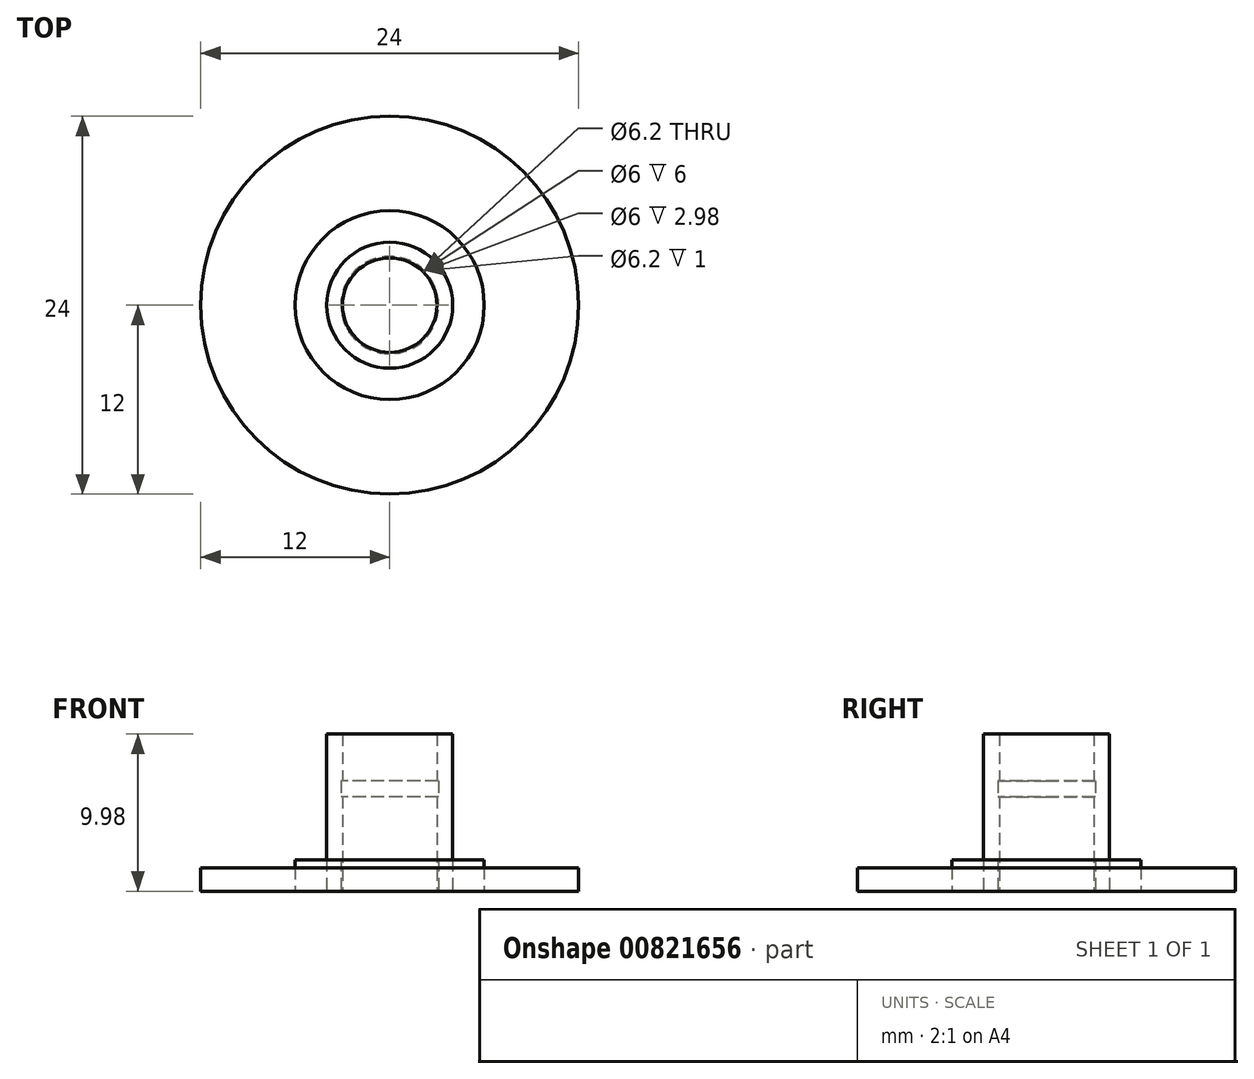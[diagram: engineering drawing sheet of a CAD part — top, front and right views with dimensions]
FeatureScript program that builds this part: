
annotation { "Feature Type Name" : "Feature", "Feature Type Description" : "" }
export const myFeature = defineFeature(function(context is Context, id is Id, definition is map)
    precondition{}
    {
        {
            var Q0;
            Q0=qCreatedBy(makeId("Top.planeOp"),FACE);
            var sketch = newSketch(context, id + "F0", { "sketchPlane" : qUnion([Q0])});
            skCircle(sketch, "E0", {"center": v(0, 0) * mm, "radius": 12 * mm});
            skCircle(sketch, "E1", {"center": v(0, 0) * mm, "radius": 3 * mm});
            skCircle(sketch, "E2", {"center": v(0, 0) * mm, "radius": 4 * mm});
            skCircle(sketch, "E3", {"center": v(0, 0) * mm, "radius": 6 * mm});
            skLineSegment(sketch, "E4", {"start": v(0, 0) * mm, "end": v(5.26, 2.9) * mm});
            skLineSegment(sketch, "E5", {"start": v(5.26, 2.9) * mm, "end": v(0, 0) * mm});
            skLineSegment(sketch, "E6", {"start": v(0, 0) * mm, "end": v(4.01, 4.46) * mm});
            skCircle(sketch, "E7", {"center": v(0, 0) * mm, "radius": 3.1 * mm});
            skSolve(sketch);
        }
        {
            var Q0;
            Q0=makeQuery(id+"F0.imprint","IMPRINT",FACE,{"disambiguationData":[TD([[makeQuery(id+"F0.imprint","IMPRINT",EDGE,{"derivedFrom":sQuery(id+"F0.wireOp",EDGE,"E0")}),1.0]])]});
            var Q1;
            Q1=makeQuery(id+"F0.imprint","IMPRINT",FACE,{"disambiguationData":[TD([[makeQuery(id+"F0.imprint","IMPRINT",EDGE,{"derivedFrom":sQuery(id+"F0.wireOp",EDGE,"E2")}),-1.0]])]});
            var Q2;
            Q2=makeQuery(id+"F0.imprint","IMPRINT",FACE,{"disambiguationData":[TD([[makeQuery(id+"F0.imprint","IMPRINT",EDGE,{"derivedFrom":sQuery(id+"F0.wireOp",EDGE,"E1")}),-1.0]])]});
            var Q3;
            Q3=makeQuery(id+"F0.imprint","IMPRINT",FACE,{"disambiguationData":[TD([[makeQuery(id+"F0.imprint","IMPRINT",EDGE,{"derivedFrom":sQuery(id+"F0.wireOp",EDGE,"E1")}),1.0]])]});
            var Q4;
            {var subQ0=sQuery(id+"F0.wireOp",EDGE,"E5");var subQ1=sQuery(id+"F0.wireOp",EDGE,"E2");var subQ2=makeQuery(id+"F0.imprint","INTERSECT",VERTEX,{"derivedFrom":[subQ1,subQ0]});Q4=makeQuery(id+"F0.imprint","IMPRINT",FACE,{"disambiguationData":[TD([[makeQuery(id+"F0.imprint","IMPRINT",EDGE,{"disambiguationData":[TD([[subQ2,1.0]])],"derivedFrom":subQ1}),1.0]])]});}
            var Q5;
            {var subQ0=sQuery(id+"F0.wireOp",EDGE,"E5");var subQ1=sQuery(id+"F0.wireOp",EDGE,"E2");var subQ2=makeQuery(id+"F0.imprint","INTERSECT",VERTEX,{"derivedFrom":[subQ1,subQ0]});Q5=makeQuery(id+"F0.imprint","IMPRINT",FACE,{"disambiguationData":[TD([[makeQuery(id+"F0.imprint","IMPRINT",EDGE,{"disambiguationData":[TD([[subQ2,-1.0]])],"derivedFrom":subQ1}),1.0]])]});}
            extrude(context, id + "F1", {"entities" : qUnion([Q0, Q1, Q2, Q3, Q4, Q5]), "depth" : 1.5 * mm, "offsetDistance" : 25 * mm});
        }
        {
            var Q0;
            Q0=makeQuery(id+"F0.imprint","IMPRINT",FACE,{"disambiguationData":[TD([[makeQuery(id+"F0.imprint","IMPRINT",EDGE,{"derivedFrom":sQuery(id+"F0.wireOp",EDGE,"E2")}),-1.0]])]});
            var Q1;
            {var subQ0=sQuery(id+"F0.wireOp",EDGE,"E5");var subQ1=sQuery(id+"F0.wireOp",EDGE,"E2");var subQ2=makeQuery(id+"F0.imprint","INTERSECT",VERTEX,{"derivedFrom":[subQ1,subQ0]});Q1=makeQuery(id+"F0.imprint","IMPRINT",FACE,{"disambiguationData":[TD([[makeQuery(id+"F0.imprint","IMPRINT",EDGE,{"disambiguationData":[TD([[subQ2,1.0]])],"derivedFrom":subQ1}),1.0]])]});}
            var Q2;
            {var subQ0=sQuery(id+"F0.wireOp",EDGE,"E5");var subQ1=sQuery(id+"F0.wireOp",EDGE,"E2");var subQ2=makeQuery(id+"F0.imprint","INTERSECT",VERTEX,{"derivedFrom":[subQ1,subQ0]});Q2=makeQuery(id+"F0.imprint","IMPRINT",FACE,{"disambiguationData":[TD([[makeQuery(id+"F0.imprint","IMPRINT",EDGE,{"disambiguationData":[TD([[subQ2,-1.0]])],"derivedFrom":subQ1}),1.0]])]});}
            extrude(context, id + "F2", {"entities" : qUnion([Q0, Q1, Q2]), "depth" : 2 * mm, "offsetDistance" : 25 * mm});
        }
        {
            var Q0;
            {var subQ0=sQuery(id+"F0.wireOp",EDGE,"E5");var subQ1=sQuery(id+"F0.wireOp",EDGE,"E1");var subQ2=makeQuery(id+"F0.imprint","INTERSECT",VERTEX,{"derivedFrom":[subQ1,subQ0]});Q0=makeQuery(id+"F0.imprint","IMPRINT",FACE,{"disambiguationData":[TD([[makeQuery(id+"F0.imprint","IMPRINT",EDGE,{"disambiguationData":[TD([[subQ2,1.0]])],"derivedFrom":subQ1}),-1.0]])]});}
            var Q1;
            {var subQ0=sQuery(id+"F0.wireOp",EDGE,"E5");var subQ1=sQuery(id+"F0.wireOp",EDGE,"E2");var subQ2=makeQuery(id+"F0.imprint","INTERSECT",VERTEX,{"derivedFrom":[subQ1,subQ0]});Q1=makeQuery(id+"F0.imprint","IMPRINT",FACE,{"disambiguationData":[TD([[makeQuery(id+"F0.imprint","IMPRINT",EDGE,{"disambiguationData":[TD([[subQ2,1.0]])],"derivedFrom":subQ1}),1.0]])]});}
            extrude(context, id + "F3", {"entities" : qUnion([Q0, Q1]), "depth" : 9.98 * mm, "offsetDistance" : 25 * mm});
        }
        {
            var Q0;
            {var subQ0=sQuery(id+"F0.wireOp",EDGE,"E5");var subQ1=sQuery(id+"F0.wireOp",EDGE,"E1");var subQ2=makeQuery(id+"F0.imprint","INTERSECT",VERTEX,{"derivedFrom":[subQ1,subQ0]});Q0=makeQuery(id+"F0.imprint","IMPRINT",FACE,{"disambiguationData":[TD([[makeQuery(id+"F0.imprint","IMPRINT",EDGE,{"disambiguationData":[TD([[subQ2,1.0]])],"derivedFrom":subQ1}),-1.0]])]});}
            extrude(context, id + "F4", {"entities" : qUnion([Q0]), "depth" : 1 * mm, "offsetDistance" : 25 * mm});
        }
        {
            var Q0;
            Q0=makeQuery(id+"F4.opExtrude","SWEPT_BODY",BODY,{"disambiguationData":[OSD([sQuery(id+"F0.wireOp",EDGE,"E1"),sQuery(id+"F0.wireOp",EDGE,"E5"),sQuery(id+"F0.wireOp",EDGE,"E6"),sQuery(id+"F0.wireOp",EDGE,"E7")])]});
            var Q1;
            Q1=qCreatedBy(makeId("Top.planeOp"),FACE);
            transform(context, id + "F5", {"entities" : qUnion([Q0]), "transformType" : TransformType.TRANSLATION_DISTANCE, "transformDirection" : qUnion([Q1]), "distance" : 6 * mm, "makeCopy" : false});
        }
        {
            var Q0;
            Q0=makeQuery(id+"F4.opExtrude","SWEPT_BODY",BODY,{"disambiguationData":[OSD([sQuery(id+"F0.wireOp",EDGE,"E1"),sQuery(id+"F0.wireOp",EDGE,"E5"),sQuery(id+"F0.wireOp",EDGE,"E6"),sQuery(id+"F0.wireOp",EDGE,"E7")])]});
            var Q1;
            Q1=makeQuery(id+"F3.opExtrude","SWEPT_BODY",BODY,{"disambiguationData":[OSD([sQuery(id+"F0.wireOp",EDGE,"E1"),sQuery(id+"F0.wireOp",EDGE,"E5"),sQuery(id+"F0.wireOp",EDGE,"E6"),sQuery(id+"F0.wireOp",EDGE,"E7")])]});
            booleanBodies(context, id + "F6", {"operationType" : BooleanOperationType.SUBTRACTION, "tools" : qUnion([Q0]), "targets" : qUnion([Q1])});
        }
    });
